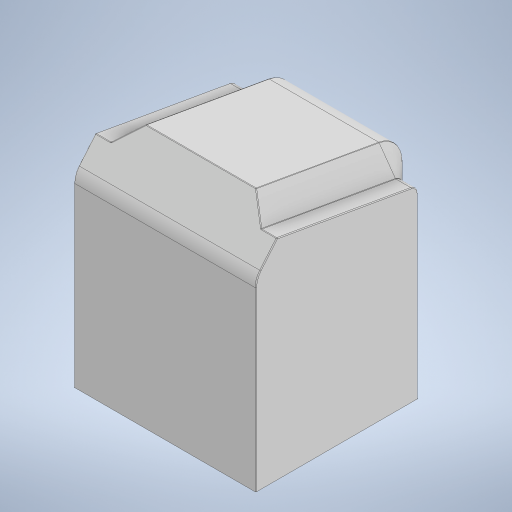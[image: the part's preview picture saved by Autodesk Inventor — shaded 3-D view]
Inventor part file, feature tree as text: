
AUTODESK INVENTOR PART (.ipt)
format: ipt  version: 2024 (Build 280153000, 153)  size: 348,160 bytes
history: native  units: mm
features: sketch x4, fillet x4, extrude x3, projected_geometry x3, plane x2, revolve x1
ambient origin geometry x8: Origin, YZ Plane, XZ Plane, XY Plane, X Axis, Y Axis, Z Axis, Center Point
bodies: Solid1 (feature_tree)
feature tree (17):
  extrude  "Extrusion1"  Depth=460.0mm
  revolve  "Revolution1"  [1 undecoded]
  sketch  "Sketch3"  dims[d4=135.0deg d5=135.0deg]
  plane  "Work Plane4"
  extrude  "Extrusion5"  TaperAngle=135.0deg  [1 undecoded]
  extrude  "Extrusion6"  Depth=10.0mm
  fillet  "Fillet1"  Radius=13.962634mm
  fillet  "Fillet3"  [1 undecoded]
  fillet  "Fillet4"  Radius=10.0mm
  fillet  "Fillet5"  Radius=10.0mm
  sketch  "Sketch1"  dims[d0=460.0mm d1=410.0mm]
  sketch  "Sketch2"  dims[d2=40.0mm d3=40.0mm]
  projected_geometry  "Projected Loop1"
  projected_geometry  "Projected Loop2"
  plane  "Work Plane3"
  sketch  "Sketch6"  dims[d7=450.0mm d8=0.0mm d9=20.0mm d10=13.962634mm d20=-10.0mm d21=10.0mm d22=0.0mm d23=10.0mm d24=0.0mm d25=50.0mm d27=2.0mm d28=2.0mm d29=2.0mm d30=67.5deg d32=10.0mm d34=50.857864mm d35=40.0mm d36=40.0mm d37=300.0mm d38=250.0mm d39=60.0mm d40=40.0mm d41=40.0mm d42=40.0mm d43=40.0mm d44=40.0mm d45=40.0mm d46=80.0mm d47=40.0mm d48=10.0mm d50=10.0mm d51=3.0mm d52=26.0mm d53=40.0mm d54=20.0mm d55=55.0mm d56=105.0mm d57=90.0mm d58=220.0mm d59=8.0mm d60=20.0mm d61=55.0mm d62=150.0deg]
  projected_geometry  "Projected Loop4"
note: 3 required parameter values undecoded (feature->parameter linkage not recoverable at this tier; creation-order binding heuristic only, values carry confidence <= 0.55)